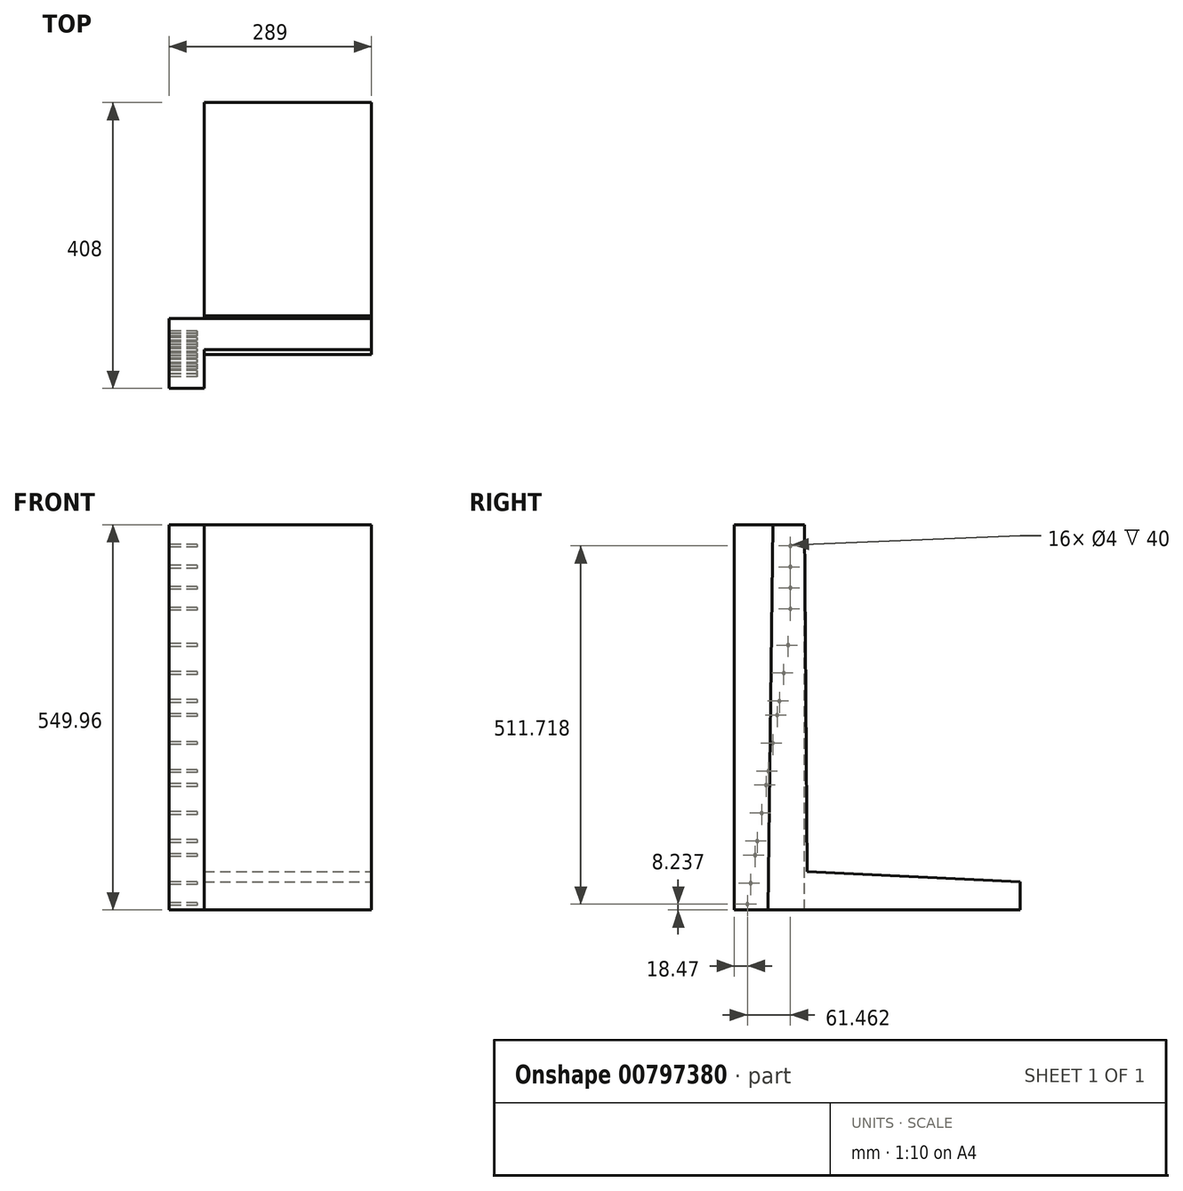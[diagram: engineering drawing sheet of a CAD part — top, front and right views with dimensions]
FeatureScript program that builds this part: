
annotation { "Feature Type Name" : "Feature", "Feature Type Description" : "" }
export const myFeature = defineFeature(function(context is Context, id is Id, definition is map)
    precondition{}
    {
        {
            var Q0;
            Q0=qCreatedBy(makeId("Right.planeOp"),FACE);
            var sketch = newSketch(context, id + "F0", { "sketchPlane" : qUnion([Q0])});
            skLineSegment(sketch, "E0", {"start": v(0.7, 0) * mm, "end": v(305, -15) * mm});
            skLineSegment(sketch, "E1", {"start": v(305, -15) * mm, "end": v(305, -55) * mm});
            skLineSegment(sketch, "E2", {"start": v(305, -55) * mm, "end": v(0, -55) * mm});
            skLineSegment(sketch, "E3", {"start": v(0, -55) * mm, "end": v(-55, -55) * mm});
            skLineSegment(sketch, "E4", {"start": v(-55, -55) * mm, "end": v(-48, 494.96) * mm});
            skLineSegment(sketch, "E5", {"start": v(-48, 494.96) * mm, "end": v(-3, 494.96) * mm});
            skLineSegment(sketch, "E6", {"start": v(-3, 494.96) * mm, "end": v(0.7, 0) * mm});
            skSolve(sketch);
        }
        {
            var Q0;
            Q0 = qSketchRegion(id + "F0", true);
            extrude(context, id + "F1", {"entities" : qUnion([Q0]), "oppositeDirection" : true, "depth" : 239 * mm, "offsetDistance" : 25 * mm});
        }
        {
            var Q0;
            Q0=qCreatedBy(makeId("Front.planeOp"),FACE);
            cPlane(context, id + "F2", {"entities" : qUnion([Q0]), "cplaneType" : CPlaneType.OFFSET, "offset" : 103 * mm, "width" : 150 * mm, "height" : 150 * mm});
        }
        {
            var Q0;
            Q0=qCreatedBy(id+"F2.planeOp",FACE);
            var sketch = newSketch(context, id + "F3", { "sketchPlane" : qUnion([Q0])});
            skLineSegment(sketch, "E7.0", {"start": v(0, -55) * mm, "end": v(0, 494.96) * mm});
            skLineSegment(sketch, "E8", {"start": v(0, -55) * mm, "end": v(50, -55) * mm});
            skLineSegment(sketch, "E9", {"start": v(50, -55) * mm, "end": v(50, 495) * mm});
            skLineSegment(sketch, "E10", {"start": v(50, 495) * mm, "end": v(0, 495) * mm});
            skLineSegment(sketch, "E11", {"start": v(0, 495) * mm, "end": v(0, -55) * mm});
            skLineSegment(sketch, "E12.0", {"start": v(-239, -55) * mm, "end": v(-239, 494.96) * mm});
            skPoint(sketch, "E13.0", {"position": v(-239, -55) * mm});
            skLineSegment(sketch, "E14", {"start": v(-239, -55) * mm, "end": v(-289, -55) * mm});
            skLineSegment(sketch, "E15", {"start": v(-289, -55) * mm, "end": v(-289, 494.96) * mm});
            skLineSegment(sketch, "E16", {"start": v(-289, 494.96) * mm, "end": v(-239, 494.96) * mm});
            skSolve(sketch);
        }
        {
            var Q0;
            Q0=makeQuery(id+"F3.imprint","IMPRINT",FACE,{"disambiguationData":[TD([[makeQuery(id+"F3.imprint","IMPRINT",EDGE,{"derivedFrom":sQuery(id+"F3.wireOp",EDGE,"E12.0")}),1.0]])]});
            extrude(context, id + "F4", {"entities" : qUnion([Q0]), "operationType" : NewBodyOperationType.ADD, "oppositeDirection" : true, "depth" : 100 * mm, "offsetDistance" : 25 * mm});
        }
        {
            var Q0;
            Q0=makeQuery(id+"F4.opExtrude","SWEPT_FACE",FACE,{"disambiguationData":[OSD([sQuery(id+"F3.wireOp",EDGE,"E15")])]});
            var sketch = newSketch(context, id + "F5", { "sketchPlane" : qUnion([Q0])});
            skLineSegment(sketch, "E17", {"start": v(3, 494.96) * mm, "end": v(23.07, 494.96) * mm});
            skLineSegment(sketch, "E18", {"start": v(23.07, 494.96) * mm, "end": v(23.07, 343.24) * mm});
            skLineSegment(sketch, "E19", {"start": v(23.07, 343.24) * mm, "end": v(85.83, -55) * mm});
            skCircle(sketch, "E20", {"center": v(23.07, 464.96) * mm, "radius": 2 * mm});
            skCircle(sketch, "E21", {"center": v(23.07, 434.96) * mm, "radius": 2 * mm});
            skCircle(sketch, "E22", {"center": v(23.07, 404.96) * mm, "radius": 2 * mm});
            skCircle(sketch, "E23", {"center": v(23.07, 374.96) * mm, "radius": 2 * mm});
            skCircle(sketch, "E24", {"center": v(26.22, 323.24) * mm, "radius": 2 * mm});
            skCircle(sketch, "E25", {"center": v(32.52, 283.24) * mm, "radius": 2 * mm});
            skCircle(sketch, "E26", {"center": v(38.83, 243.24) * mm, "radius": 2 * mm});
            skCircle(sketch, "E27", {"center": v(41.98, 223.24) * mm, "radius": 2 * mm});
            skCircle(sketch, "E28", {"center": v(48.28, 183.24) * mm, "radius": 2 * mm});
            skCircle(sketch, "E29", {"center": v(57.74, 123.24) * mm, "radius": 2 * mm});
            skCircle(sketch, "E30", {"center": v(64.04, 83.24) * mm, "radius": 2 * mm});
            skCircle(sketch, "E31", {"center": v(70.35, 43.24) * mm, "radius": 2 * mm});
            skCircle(sketch, "E32", {"center": v(73.5, 23.24) * mm, "radius": 2 * mm});
            skCircle(sketch, "E33", {"center": v(79.8, -16.76) * mm, "radius": 2 * mm});
            skCircle(sketch, "E34", {"center": v(84.53, -46.76) * mm, "radius": 2 * mm});
            skCircle(sketch, "E35", {"center": v(54.59, 143.24) * mm, "radius": 2 * mm});
            skLineSegment(sketch, "E36.0", {"start": v(3, -55) * mm, "end": v(103, -55) * mm});
            skLineSegment(sketch, "E37.0", {"start": v(103, -55) * mm, "end": v(103, 494.96) * mm});
            skSolve(sketch);
        }
        {
            var Q0;
            Q0 = qSketchRegion(id + "F5", true);
            extrude(context, id + "F6", {"entities" : qUnion([Q0]), "operationType" : NewBodyOperationType.REMOVE, "oppositeDirection" : true, "depth" : 40 * mm, "offsetDistance" : 25 * mm});
        }
    });
